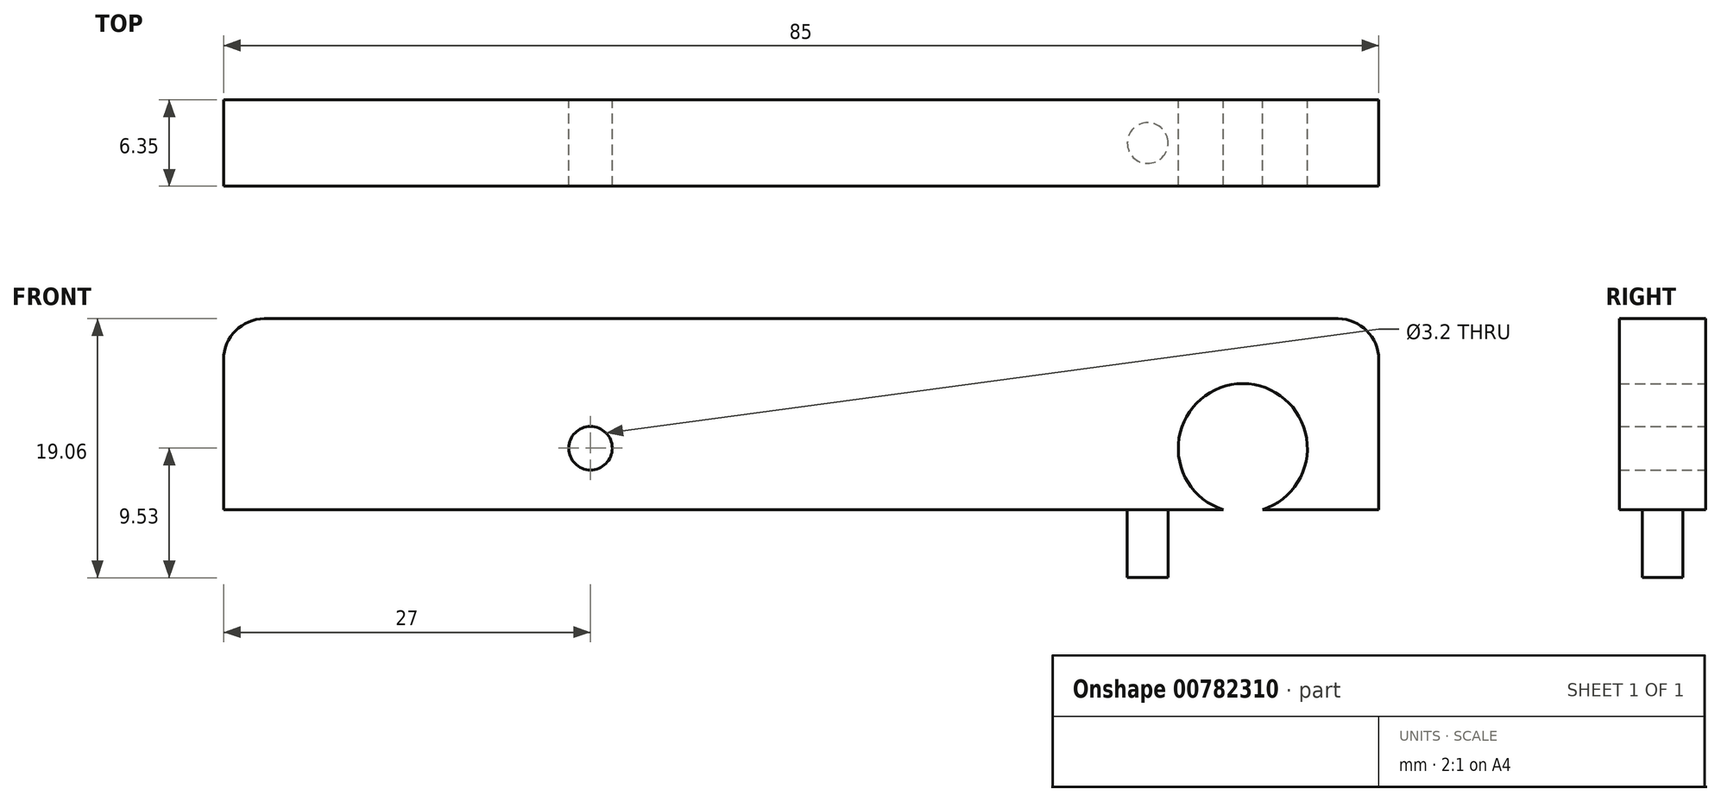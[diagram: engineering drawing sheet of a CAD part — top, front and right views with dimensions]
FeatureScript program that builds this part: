
annotation { "Feature Type Name" : "Feature", "Feature Type Description" : "" }
export const myFeature = defineFeature(function(context is Context, id is Id, definition is map)
    precondition{}
    {
        {
            var Q0;
            Q0=qCreatedBy(makeId("Front.planeOp"),FACE);
            var sketch = newSketch(context, id + "F0", { "sketchPlane" : qUnion([Q0])});
            skLineSegment(sketch, "E0.bottom", {"start": v(-42.5, 9.53) * mm, "end": v(42.5, 9.53) * mm});
            skLineSegment(sketch, "E0.top", {"start": v(-42.5, -9.53) * mm, "end": v(42.5, -9.53) * mm});
            skLineSegment(sketch, "E0.left", {"start": v(-42.5, 9.52) * mm, "end": v(-42.5, -9.53) * mm});
            skLineSegment(sketch, "E0.right", {"start": v(42.5, 9.53) * mm, "end": v(42.5, -9.52) * mm});
            skPoint(sketch, "E0.middle", {"position": v(0, 0) * mm});
            skCircle(sketch, "E1", {"center": v(32.5, 0) * mm, "radius": 4.75 * mm});
            skCircle(sketch, "E2", {"center": v(-15.5, 0) * mm, "radius": 1.6 * mm});
            skSolve(sketch);
        }
        {
            var Q0;
            Q0 = qSketchRegion(id + "F0", true);
            extrude(context, id + "F1", {"entities" : qUnion([Q0]), "depth" : 6.35 * mm, "offsetDistance" : 25 * mm});
        }
        {
            var Q0;
            Q0=makeQuery(id+"F1.opExtrude","SWEPT_FACE",FACE,{"disambiguationData":[OSD([sQuery(id+"F0.wireOp",EDGE,"E0.top")])]});
            var sketch = newSketch(context, id + "F2", { "sketchPlane" : qUnion([Q0])});
            skCircle(sketch, "E3", {"center": v(-25.5, 3.18) * mm, "radius": 1.5 * mm});
            skPoint(sketch, "E3.centerSnap0", {"position": v(-42.5, 3.17) * mm});
            skCircle(sketch, "E4.MirrorC", {"center": v(25.5, 3.18) * mm, "radius": 1.5 * mm});
            skSolve(sketch);
        }
        {
            var Q0;
            Q0=makeQuery(id+"F2.imprint","IMPRINT",FACE,{"disambiguationData":[TD([[makeQuery(id+"F2.imprint","IMPRINT",EDGE,{"derivedFrom":sQuery(id+"F2.wireOp",EDGE,"E4.MirrorC")}),-1.0]])]});
            var Q1;
            Q1=makeQuery(id+"F2.imprint","IMPRINT",FACE,{"disambiguationData":[TD([[makeQuery(id+"F2.imprint","IMPRINT",EDGE,{"derivedFrom":sQuery(id+"F2.wireOp",EDGE,"E3")}),1.0]])]});
            extrude(context, id + "F3", {"entities" : qUnion([Q0, Q1]), "operationType" : NewBodyOperationType.REMOVE, "oppositeDirection" : true, "depth" : 5 * mm, "offsetDistance" : 25 * mm});
        }
        {
            var Q0;
            Q0=makeQuery(id+"F1.opExtrude","SWEPT_EDGE",EDGE,{"disambiguationData":[OSD([sQuery(id+"F0.wireOp",EDGE,"E0.bottom"),sQuery(id+"F0.wireOp",EDGE,"E0.right")])]});
            var Q1;
            Q1=makeQuery(id+"F1.opExtrude","SWEPT_EDGE",EDGE,{"disambiguationData":[OSD([sQuery(id+"F0.wireOp",EDGE,"E0.bottom"),sQuery(id+"F0.wireOp",EDGE,"E0.left")])]});
            var Q2;
            Q2=makeQuery(id+"F1.opExtrude","SWEPT_EDGE",EDGE,{"disambiguationData":[OSD([sQuery(id+"F0.wireOp",EDGE,"E0.top"),sQuery(id+"F0.wireOp",EDGE,"E0.right")])]});
            var Q3;
            Q3=makeQuery(id+"F1.opExtrude","SWEPT_EDGE",EDGE,{"disambiguationData":[OSD([sQuery(id+"F0.wireOp",EDGE,"E0.top"),sQuery(id+"F0.wireOp",EDGE,"E0.left")])]});
            fillet(context, id + "F4", {"entities" : qUnion([Q0, Q1, Q2, Q3]), "radius" : 3 * mm, "tangentPropagation" : true, "allowEdgeOverflow" : false});
        }
    });
